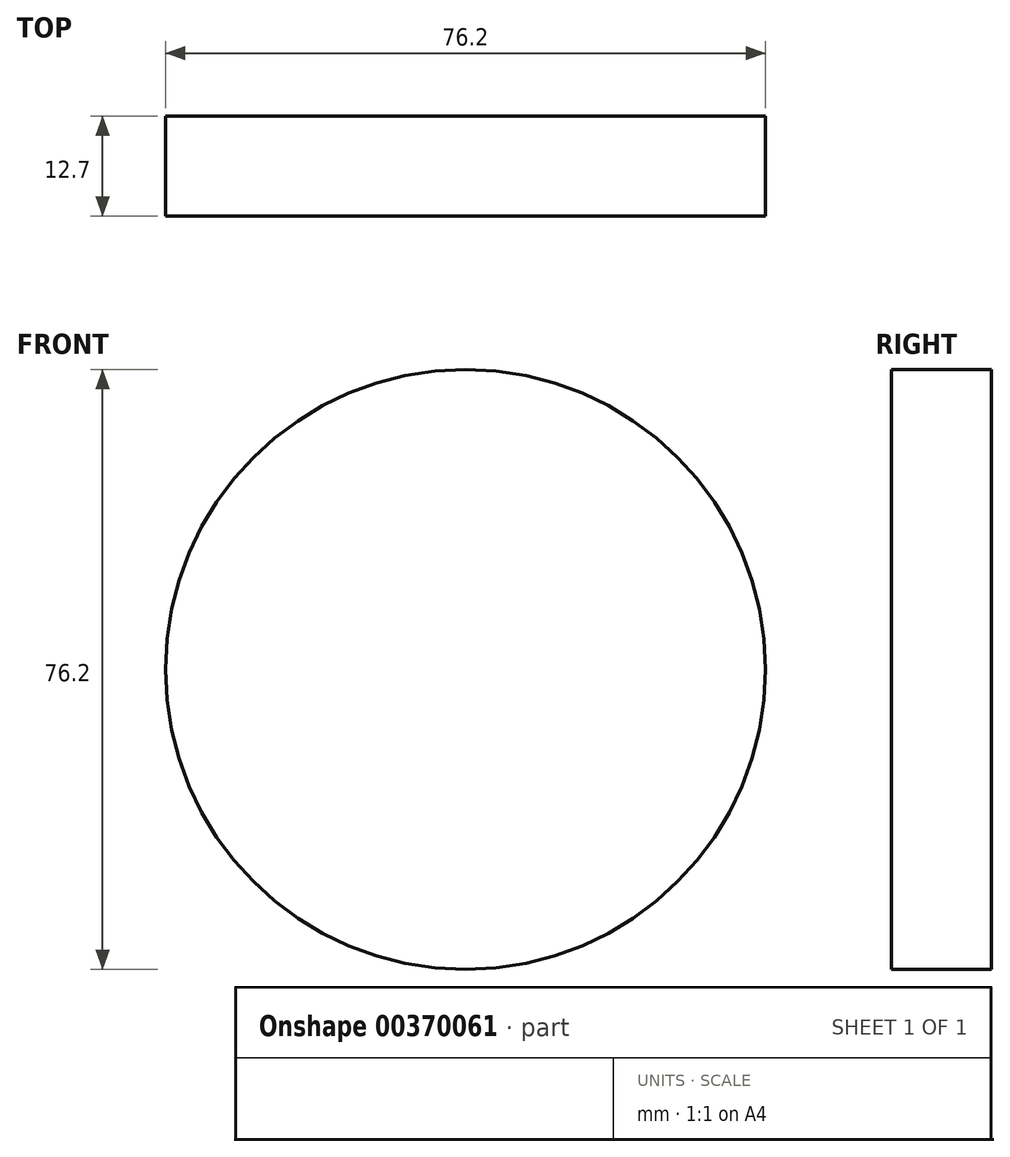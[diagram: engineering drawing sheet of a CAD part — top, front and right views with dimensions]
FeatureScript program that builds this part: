
annotation { "Feature Type Name" : "Feature", "Feature Type Description" : "" }
export const myFeature = defineFeature(function(context is Context, id is Id, definition is map)
    precondition{}
    {
        {
            var Q0;
            Q0=qCreatedBy(makeId("Front.planeOp"),FACE);
            var sketch = newSketch(context, id + "F0", { "sketchPlane" : qUnion([Q0])});
            skCircle(sketch, "E0", {"center": v(0, 0) * mm, "radius": 38.1 * mm});
            skSolve(sketch);
        }
        {
            var Q0;
            Q0=makeQuery(id+"F0.imprint","IMPRINT",FACE,{"disambiguationData":[TD([[makeQuery(id+"F0.imprint","IMPRINT",EDGE,{"derivedFrom":sQuery(id+"F0.wireOp",EDGE,"E0")}),1.0]])]});
            extrude(context, id + "F1", {"entities" : qUnion([Q0]), "depth" : 12.7 * mm});
        }
    });
